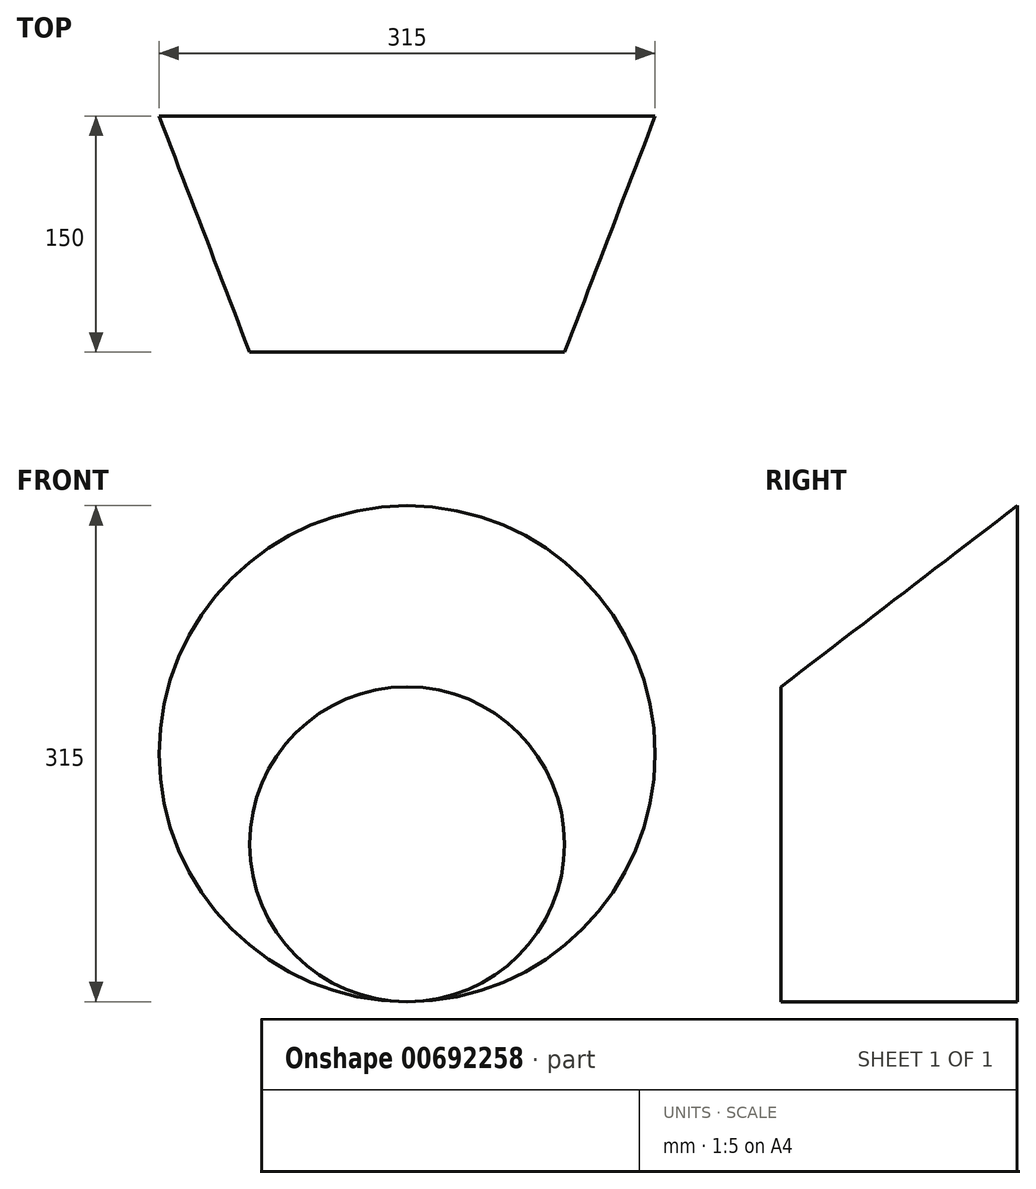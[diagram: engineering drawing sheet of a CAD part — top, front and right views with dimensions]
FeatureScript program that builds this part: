
annotation { "Feature Type Name" : "Feature", "Feature Type Description" : "" }
export const myFeature = defineFeature(function(context is Context, id is Id, definition is map)
    precondition{}
    {
        {
            var Q0;
            Q0=qCreatedBy(makeId("Front.planeOp"),FACE);
            var sketch = newSketch(context, id + "F0", { "sketchPlane" : qUnion([Q0])});
            skCircle(sketch, "E0", {"center": v(0, 0) * mm, "radius": 157.5 * mm});
            skSolve(sketch);
        }
        {
            var Q0;
            Q0=qCreatedBy(makeId("Front.planeOp"),FACE);
            cPlane(context, id + "F1", {"entities" : qUnion([Q0]), "cplaneType" : CPlaneType.OFFSET, "offset" : 150 * mm, "width" : 150 * mm, "height" : 150 * mm});
        }
        {
            var Q0;
            Q0=qCreatedBy(id+"F1.planeOp",FACE);
            var sketch = newSketch(context, id + "F2", { "sketchPlane" : qUnion([Q0])});
            skCircle(sketch, "E1", {"center": v(0, -57.5) * mm, "radius": 100 * mm});
            skSolve(sketch);
        }
        {
            var Q0;
            Q0 = qSketchRegion(id + "F0", true);
            var Q1;
            Q1 = qSketchRegion(id + "F2", true);
            loft(context, id + "F3", {"sheetProfilesArray" : [{ "sheetProfileEntities" : qUnion([Q0]) }, { "sheetProfileEntities" : qUnion([Q1]) }]});
        }
    });
